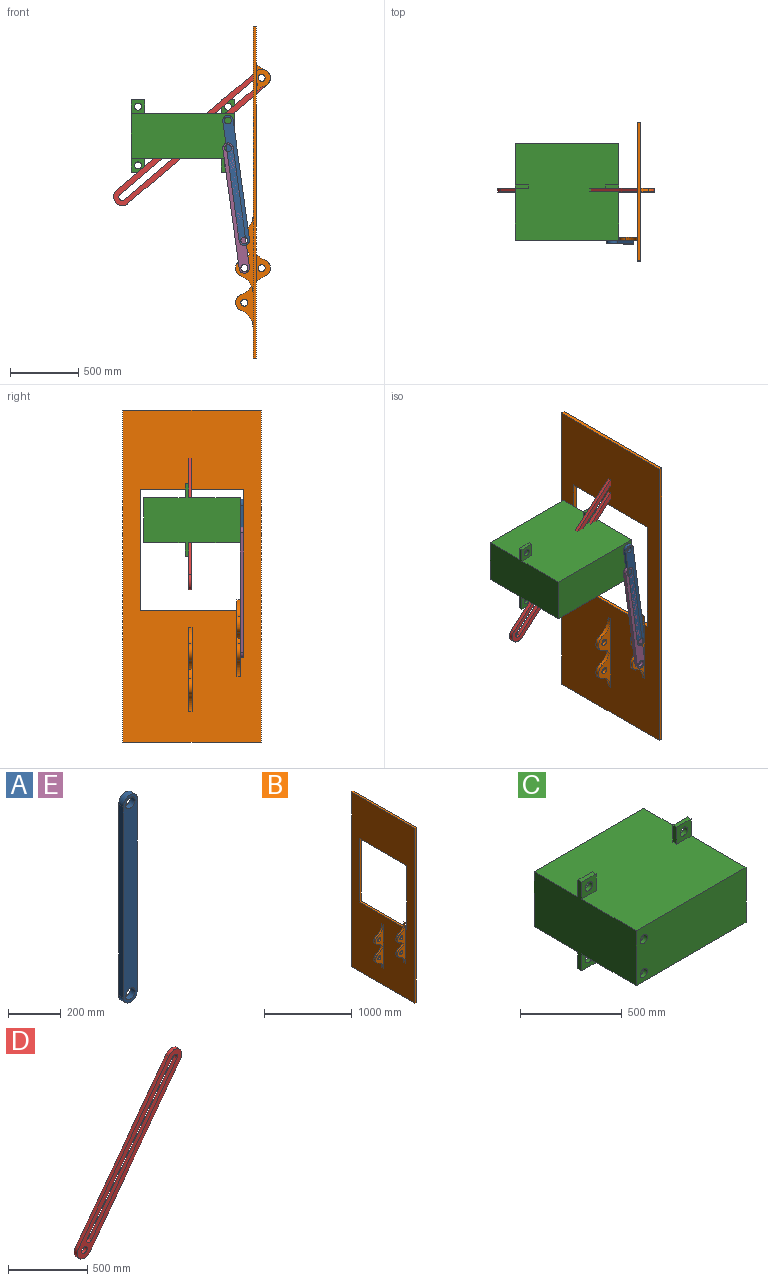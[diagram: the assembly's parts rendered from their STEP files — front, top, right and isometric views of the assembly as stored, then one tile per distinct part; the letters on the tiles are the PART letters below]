
ASSEMBLY  parts=5 mates=7
PART A: 8 faces, bbox 76.2x25.4x965.2 mm
  f0: plane 889x25.4mm, normal (1,0,0), area 22580.6mm2, adj f1,f3,f6,f7
  f1: cylinder r=38.1mm len=76.2mm, axis (0,1,0), area 3040.2mm2, adj f0,f2,f6,f7
  f2: plane 889x25.4mm, normal (-1,0,0), area 22580.6mm2, adj f1,f3,f6,f7
  f3: cylinder r=38.1mm len=76.2mm, axis (0,1,0), area 3040.2mm2, adj f0,f2,f6,f7
  f4: cylinder r=25.4mm len=50.8mm, axis (0,1,0), area 4053.7mm2, adj f6,f7
  f5: cylinder r=25.4mm len=50.8mm, axis (0,1,0), area 4053.7mm2, adj f6,f7
  f6: plane 965.2x76.2mm, normal (0,-1,0), area 68248.5mm2, adj f0,f1,f2,f3,f4,f5
  f7: plane 965.2x76.2mm, normal (0,1,0), area 68248.5mm2, adj f0,f1,f2,f3,f4,f5
PART B: 43 faces, bbox 254x1016x2438.4 mm
  f0: plane 2438.4x1016mm, normal (-1,0,0), area 1772117mm2, adj f2,f3,f4,f5,f6,f7,f8,f12
  f1: plane 2438.4x1016mm, normal (1,0,0), area 1789490.4mm2, adj f2,f3,f4,f5,f6,f7,f18,f20
  f2: plane 1016x25.4mm, normal (0,0,1), area 25806.4mm2, adj f0,f1,f3,f7
  f3: plane 2438.4x25.4mm, normal (0,-1,0), area 61935.4mm2, adj f0,f1,f2,f4
  f4: plane 1016x25.4mm, normal (0,0,-1), area 25806.4mm2, adj f0,f1,f3,f7
  f5: plane 889x25.4mm, normal (0,1,0), area 22580.6mm2, adj f0,f1,f18,f20
  f6: plane 889x25.4mm, normal (0,-1,0), area 22580.6mm2, adj f0,f1,f18,f20
  f7: plane 2438.4x25.4mm, normal (0,1,0), area 61935.4mm2, adj f0,f1,f2,f4
  f8: cylinder r=127mm len=119.74mm, axis (0,-1,0), area 3970.8mm2, adj f0,f9,f12,f13
  f9: cylinder r=63.5mm len=119.74mm, axis (0,-1,0), area 3970.8mm2, adj f8,f10,f12,f13
  f10: cylinder r=127mm len=57.89mm, axis (0,-1,0), area 1837.3mm2, adj f9,f12,f13,f14
  f11: cylinder r=25.4mm len=50.8mm, axis (0,-1,0), area 4053.7mm2, adj f12,f13
  f12: plane 562.41x127mm, normal (0,1,0), area 33266.7mm2, adj f0,f8,f9,f10,f11,f14,f15,f16
  f13: plane 562.41x127mm, normal (0,-1,0), area 33266.7mm2, adj f0,f8,f9,f10,f11,f14,f15,f16
  f14: cylinder r=127mm len=57.89mm, axis (0,-1,0), area 1837.3mm2, adj f10,f12,f13,f15
  f15: cylinder r=63.5mm len=119.74mm, axis (0,-1,0), area 3970.8mm2, adj f12,f13,f14,f16
  f16: cylinder r=127mm len=119.74mm, axis (0,-1,0), area 3970.8mm2, adj f12,f13,f15,f19
  f17: cylinder r=25.4mm len=50.8mm, axis (0,-1,0), area 4053.7mm2, adj f12,f13
  f18: plane 762x25.4mm, normal (0,0,-1), area 19354.8mm2, adj f0,f1,f5,f6
  f19: plane 78.01x25.4mm, normal (1,0,0), area 1981.3mm2, adj f12,f13,f16,f20
  f20: plane 762x25.4mm, normal (0,0,1), area 19354.8mm2, adj f0,f1,f5,f6,f19
  f21: cylinder r=127mm len=73.26mm, axis (0,-1,0), area 2593.2mm2, adj f22,f25,f26,f29
  f22: cylinder r=63.5mm len=119.74mm, axis (0,-1,0), area 3970.8mm2, adj f21,f23,f25,f26
  f23: cylinder r=127mm len=119.74mm, axis (0,-1,0), area 3970.8mm2, adj f0,f22,f25,f26
  f24: cylinder r=25.4mm len=50.8mm, axis (0,-1,0), area 4053.7mm2, adj f25,f26
  f25: plane 613.21x127mm, normal (0,1,0), area 34202.1mm2, adj f0,f21,f22,f23,f24,f27,f28,f29
  f26: plane 613.21x127mm, normal (0,-1,0), area 34202.1mm2, adj f0,f21,f22,f23,f24,f27,f28,f29
  f27: cylinder r=127mm len=119.74mm, axis (0,-1,0), area 3970.8mm2, adj f0,f25,f26,f28
  f28: cylinder r=63.5mm len=119.74mm, axis (0,-1,0), area 3970.8mm2, adj f25,f26,f27,f29
  f29: cylinder r=127mm len=73.26mm, axis (0,-1,0), area 2593.2mm2, adj f21,f25,f26,f28
  f30: cylinder r=25.4mm len=50.8mm, axis (0,-1,0), area 4053.7mm2, adj f25,f26
  f31: plane 206.81x101.6mm, normal (0,1,0), area 10810.5mm2, adj f1,f33,f34,f35,f36
  f32: plane 206.81x101.6mm, normal (0,-1,0), area 10810.5mm2, adj f1,f33,f34,f35,f36
  f33: cylinder r=127mm len=59.27mm, axis (0,-1,0), area 1895mm2, adj f1,f31,f32,f36
  f34: cylinder r=127mm len=59.27mm, axis (0,-1,0), area 1895mm2, adj f1,f31,f32,f36
  f35: cylinder r=25.4mm len=50.8mm, axis (0,-1,0), area 4053.7mm2, adj f31,f32
  f36: cylinder r=63.5mm len=119.74mm, axis (0,-1,0), area 3970.8mm2, adj f31,f32,f33,f34
  f37: cylinder r=127mm len=59.27mm, axis (0,-1,0), area 1895mm2, adj f1,f40,f41,f42
  f38: cylinder r=127mm len=59.27mm, axis (0,-1,0), area 1895mm2, adj f1,f40,f41,f42
  f39: cylinder r=25.4mm len=50.8mm, axis (0,-1,0), area 4053.7mm2, adj f41,f42
  f40: cylinder r=63.5mm len=119.74mm, axis (0,-1,0), area 3970.8mm2, adj f37,f38,f41,f42
  f41: plane 206.81x101.6mm, normal (0,1,0), area 10810.5mm2, adj f1,f37,f38,f39,f40
  f42: plane 206.81x101.6mm, normal (0,-1,0), area 10810.5mm2, adj f1,f37,f38,f39,f40
PART C: 30 faces, bbox 762x711.2x533.4 mm
  f0: plane 762x711.2mm, normal (0,0,1), area 536773.1mm2, adj f1,f3,f4,f5,f17,f18,f19,f26
  f1: plane 762x330.2mm, normal (0,1,0), area 251612.4mm2, adj f0,f2,f4,f5
  f2: plane 762x711.2mm, normal (0,0,-1), area 536773.1mm2, adj f1,f3,f4,f5,f12,f13,f14,f20
  f3: plane 762x330.2mm, normal (0,-1,0), area 247558.7mm2, adj f0,f2,f4,f5,f6,f8
  f4: plane 711.2x533.4mm, normal (-1,0,0), area 239999.5mm2, adj f0,f1,f2,f3,f21,f23,f24,f25
  f5: plane 711.2x533.4mm, normal (1,0,0), area 239999.5mm2, adj f0,f1,f2,f3,f10,f13,f14,f15
  f6: cylinder r=25.4mm len=50.8mm, axis (0,-1,0), area 4053.7mm2, adj f3,f7
  f7: plane 50.8x50.8mm, normal (0,-1,0), area 2026.8mm2, adj f6
  f8: cylinder r=25.4mm len=50.8mm, axis (0,-1,0), area 4053.7mm2, adj f3,f9
  f9: plane 50.8x50.8mm, normal (0,-1,0), area 2026.8mm2, adj f8
  f10: plane 101.6x25.4mm, normal (0,0,-1), area 2580.6mm2, adj f5,f12,f13,f14
  f11: cylinder r=25.4mm len=50.8mm, axis (0,-1,0), area 4053.7mm2, adj f13,f14
  f12: plane 101.6x25.4mm, normal (-1,0,0), area 2580.6mm2, adj f2,f10,f13,f14
  f13: plane 101.6x101.6mm, normal (0,1,0), area 8295.7mm2, adj f2,f5,f10,f11,f12
  f14: plane 101.6x101.6mm, normal (0,-1,0), area 8295.7mm2, adj f2,f5,f10,f11,f12
  f15: plane 101.6x25.4mm, normal (0,0,1), area 2580.6mm2, adj f5,f17,f18,f19
  f16: cylinder r=25.4mm len=50.8mm, axis (0,-1,0), area 4053.7mm2, adj f18,f19
  f17: plane 101.6x25.4mm, normal (-1,0,0), area 2580.6mm2, adj f0,f15,f18,f19
  f18: plane 101.6x101.6mm, normal (0,1,0), area 8295.7mm2, adj f0,f5,f15,f16,f17
  f19: plane 101.6x101.6mm, normal (0,-1,0), area 8295.7mm2, adj f0,f5,f15,f16,f17
  f20: plane 101.6x25.4mm, normal (1,0,0), area 2580.6mm2, adj f2,f21,f23,f24
  f21: plane 101.6x25.4mm, normal (0,0,-1), area 2580.6mm2, adj f4,f20,f23,f24
  f22: cylinder r=25.4mm len=50.8mm, axis (0,-1,0), area 4053.7mm2, adj f23,f24
  f23: plane 101.6x101.6mm, normal (0,1,0), area 8295.7mm2, adj f2,f4,f20,f21,f22
  f24: plane 101.6x101.6mm, normal (0,-1,0), area 8295.7mm2, adj f2,f4,f20,f21,f22
  f25: plane 101.6x25.4mm, normal (0,0,1), area 2580.6mm2, adj f4,f26,f28,f29
  f26: plane 101.6x25.4mm, normal (1,0,0), area 2580.6mm2, adj f0,f25,f28,f29
  f27: cylinder r=25.4mm len=50.8mm, axis (0,-1,0), area 4053.7mm2, adj f28,f29
  f28: plane 101.6x101.6mm, normal (0,1,0), area 8295.7mm2, adj f0,f4,f25,f26,f27
  f29: plane 101.6x101.6mm, normal (0,-1,0), area 8295.7mm2, adj f0,f4,f25,f26,f27
PART D: 11 faces, bbox 930.4x25.4x1207.2 mm
  f0: cylinder r=63.5mm len=114.45mm, axis (0,-1,0), area 5067.1mm2, adj f1,f8,f9,f10
  f1: plane 1080.2x803.38mm, normal (-0.8,0,0.6), area 34193.5mm2, adj f0,f2,f9,f10
  f2: cylinder r=63.5mm len=114.45mm, axis (0,-1,0), area 5067.1mm2, adj f1,f8,f9,f10
  f3: plane 1019.06x757.91mm, normal (-0.8,0,0.6), area 32258mm2, adj f4,f7,f9,f10
  f4: cylinder r=25.4mm len=45.78mm, axis (0,-1,0), area 2026.8mm2, adj f3,f5,f9,f10
  f5: plane 1019.06x757.91mm, normal (0.8,0,-0.6), area 32258mm2, adj f4,f7,f9,f10
  f6: cylinder r=25.4mm len=50.8mm, axis (0,-1,0), area 4053.7mm2, adj f9,f10
  f7: cylinder r=25.4mm len=45.78mm, axis (0,-1,0), area 2026.8mm2, adj f3,f5,f9,f10
  f8: plane 1080.2x803.38mm, normal (0.8,0,-0.6), area 34193.5mm2, adj f0,f2,f9,f10
  f9: plane 1207.2x930.38mm, normal (0,1,0), area 115065.4mm2, adj f0,f1,f2,f3,f4,f5,f6,f7
  f10: plane 1207.2x930.38mm, normal (0,-1,0), area 115065.4mm2, adj f0,f1,f2,f3,f4,f5,f6,f7
PART E: same geometry as A
PLACE A rot(axis=(0,-1,0),7.8deg) t=(448.85,578.68,464.1)mm
PLACE B t=(-247.28,578.68,-93.04)mm fixed
PLACE C rot(axis=(0,-1,0),180deg) t=(-1142.24,578.68,2946.79)mm
PLACE D rot(axis=(0,-1,0),167.2deg) t=(-155.42,223.08,2374.72)mm
PLACE E rot(axis=(0,-1,0),7.8deg) t=(448.85,578.68,260.9)mm
MATE revolute B.f9 <-> E.f3  axis (0,-1,0) through (-310.78,223.08,567.36)mm
MATE revolute A.f1 <-> C.f6  axis (0,1,0) through (-431.04,223.08,1651.39)mm
MATE revolute E.f1 <-> C.f8  axis (0,1,0) through (-431.04,223.08,1448.19)mm
MATE revolute D.f0 <-> B.f39  axis (0,-1,0) through (-183.78,591.38,1964.36)mm
MATE parallel C.f2 <-> B.f2  axis (0,0,1) through (-761.24,578.31,1702.19)mm
MATE planar C.f3 <-> E.f7  axis (0,-1,0) through (-766.64,223.08,1536.89)mm
MATE revolute A.f3 <-> B.f15  axis (0,1,0) through (-310.78,223.08,770.56)mm
